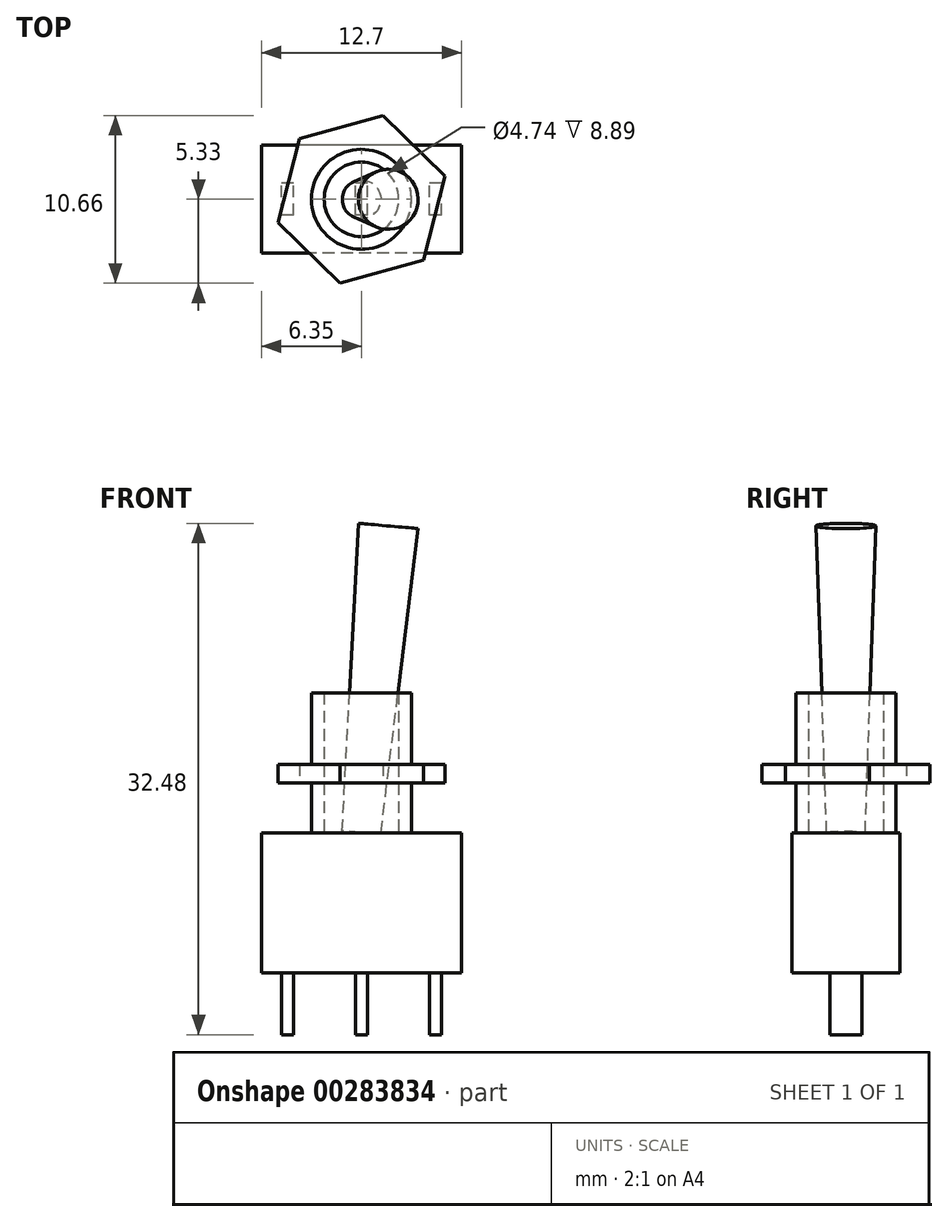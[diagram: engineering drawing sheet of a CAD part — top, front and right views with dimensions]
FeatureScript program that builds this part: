
annotation { "Feature Type Name" : "Feature", "Feature Type Description" : "" }
export const myFeature = defineFeature(function(context is Context, id is Id, definition is map)
    precondition{}
    {
        {
            var Q0;
            Q0=qCreatedBy(makeId("Top.planeOp"),FACE);
            var sketch = newSketch(context, id + "F0", { "sketchPlane" : qUnion([Q0])});
            skCircle(sketch, "E0", {"center": v(0, 0) * mm, "radius": 3.18 * mm});
            skCircle(sketch, "E1", {"center": v(0, 0) * mm, "radius": 2.37 * mm});
            skSolve(sketch);
        }
        {
            var Q0;
            Q0=makeQuery(id+"F0.imprint","IMPRINT",FACE,{"disambiguationData":[TD([[makeQuery(id+"F0.imprint","IMPRINT",EDGE,{"derivedFrom":sQuery(id+"F0.wireOp",EDGE,"E0")}),1.0]])]});
            extrude(context, id + "F1", {"entities" : qUnion([Q0]), "depth" : 8.9 * mm});
        }
        {
            var Q0;
            Q0=makeQuery(id+"F1.opExtrude","CAP_FACE",FACE,{"disambiguationData":[OSD([sQuery(id+"F0.wireOp",EDGE,"E0"),sQuery(id+"F0.wireOp",EDGE,"E1")])],"isStart":true});
            var sketch = newSketch(context, id + "F2", { "sketchPlane" : qUnion([Q0])});
            skLineSegment(sketch, "E2.bottom", {"start": v(6.35, -3.43) * mm, "end": v(-6.35, -3.43) * mm});
            skLineSegment(sketch, "E2.top", {"start": v(6.35, 3.43) * mm, "end": v(-6.35, 3.43) * mm});
            skLineSegment(sketch, "E2.left", {"start": v(6.35, -3.43) * mm, "end": v(6.35, 3.43) * mm});
            skLineSegment(sketch, "E2.right", {"start": v(-6.35, -3.43) * mm, "end": v(-6.35, 3.43) * mm});
            skPoint(sketch, "E2.middle", {"position": v(0, 0) * mm});
            skSolve(sketch);
        }
        {
            var Q0;
            Q0 = qSketchRegion(id + "F2", true);
            extrude(context, id + "F3", {"entities" : qUnion([Q0]), "operationType" : NewBodyOperationType.ADD, "depth" : 8.9 * mm});
        }
        {
            var Q0;
            Q0=makeQuery(id+"F3.opExtrude","CAP_FACE",FACE,{"disambiguationData":[OSD([sQuery(id+"F2.wireOp",EDGE,"E2.bottom"),sQuery(id+"F2.wireOp",EDGE,"E2.top"),sQuery(id+"F2.wireOp",EDGE,"E2.left"),sQuery(id+"F2.wireOp",EDGE,"E2.right")])],"isStart":false});
            var sketch = newSketch(context, id + "F4", { "sketchPlane" : qUnion([Q0])});
            skLineSegment(sketch, "E3.bottom", {"start": v(-4.32, 1.02) * mm, "end": v(-5.08, 1.02) * mm});
            skLineSegment(sketch, "E3.top", {"start": v(-4.32, -1.02) * mm, "end": v(-5.08, -1.02) * mm});
            skLineSegment(sketch, "E3.left", {"start": v(-4.32, 1.02) * mm, "end": v(-4.32, -1.02) * mm});
            skLineSegment(sketch, "E3.right", {"start": v(-5.08, 1.02) * mm, "end": v(-5.08, -1.02) * mm});
            skPoint(sketch, "E3.middle", {"position": v(0, 0) * mm});
            skPoint(sketch, "E3.middle.positionSnap0", {"position": v(-6.35, 0) * mm});
            skPoint(sketch, "E3.middle.positionSnap1", {"position": v(0, 3.43) * mm});
            skPoint(sketch, "E3.centerSnap0", {"position": v(-6.35, 0) * mm});
            skPoint(sketch, "E3.centerSnap1", {"position": v(0, 3.43) * mm});
            skLineSegment(sketch, "E4.1.0.0", {"start": v(-0.38, 1.02) * mm, "end": v(-0.38, -1.02) * mm});
            skLineSegment(sketch, "E4.1.0.1", {"start": v(0.38, 1.02) * mm, "end": v(0.38, -1.02) * mm});
            skLineSegment(sketch, "E4.1.0.2", {"start": v(0.38, -1.02) * mm, "end": v(-0.38, -1.02) * mm});
            skLineSegment(sketch, "E4.1.0.3", {"start": v(0.38, 1.02) * mm, "end": v(-0.38, 1.02) * mm});
            skPoint(sketch, "E4.1.0.4", {"position": v(4.7, 0) * mm});
            skLineSegment(sketch, "E4.2.0.0", {"start": v(4.32, 1.02) * mm, "end": v(4.32, -1.02) * mm});
            skLineSegment(sketch, "E4.2.0.1", {"start": v(5.08, 1.02) * mm, "end": v(5.08, -1.02) * mm});
            skLineSegment(sketch, "E4.2.0.2", {"start": v(5.08, -1.02) * mm, "end": v(4.32, -1.02) * mm});
            skLineSegment(sketch, "E4.2.0.3", {"start": v(5.08, 1.02) * mm, "end": v(4.32, 1.02) * mm});
            skPoint(sketch, "E4.2.0.4", {"position": v(9.4, 0) * mm});
            skLineSegment(sketch, "E4.direction1", {"start": v(-5.08, -1.02) * mm, "end": v(-0.38, -1.02) * mm, "construction": true});
            skLineSegment(sketch, "E5", {"start": v(0, 3.43) * mm, "end": v(0, 1.02) * mm, "construction": true});
            skLineSegment(sketch, "E6", {"start": v(0, -3.43) * mm, "end": v(0, -1.02) * mm, "construction": true});
            skSolve(sketch);
        }
        {
            var Q0;
            Q0 = qSketchRegion(id + "F4", true);
            extrude(context, id + "F5", {"entities" : qUnion([Q0]), "operationType" : NewBodyOperationType.ADD, "depth" : 3.94 * mm});
        }
        {
            var Q0;
            {var subQ0=sQuery(id+"F2.wireOp",EDGE,"E2.left");var subQ1=sQuery(id+"F2.wireOp",EDGE,"E2.top");var subQ2=sQuery(id+"F2.wireOp",EDGE,"E2.bottom");var subQ3=sQuery(id+"F2.wireOp",EDGE,"E2.right");Q0=makeQuery(id+"F3.boolean.opBoolean","SPLIT",FACE,{"disambiguationData":[TD([makeQuery(id+"F1.opExtrude","SWEPT_FACE",FACE,{"disambiguationData":[OSD([sQuery(id+"F0.wireOp",EDGE,"E0")])]})])],"derivedFrom":makeQuery(id+"F3.opExtrude","CAP_FACE",FACE,{"disambiguationData":[OSD([subQ2,subQ1,subQ0,subQ3])],"isStart":true})});}
            cPlane(context, id + "F6", {"entities" : qUnion([Q0]), "cplaneType" : CPlaneType.OFFSET, "offset" : 3.17 * mm, "width" : 152.4 * mm, "height" : 152.4 * mm});
        }
        {
            var Q0;
            Q0=qCreatedBy(id+"F6.planeOp",FACE);
            var sketch = newSketch(context, id + "F7", { "sketchPlane" : qUnion([Q0])});
            skCircle(sketch, "E7.cCircle", {"center": v(0, 0) * mm, "radius": 4.76 * mm, "construction": true});
            skLineSegment(sketch, "E7.0", {"start": v(-1.37, -5.33) * mm, "end": v(-5.3, -1.48) * mm});
            skLineSegment(sketch, "E7.1", {"start": v(-5.3, -1.48) * mm, "end": v(-3.93, 3.85) * mm});
            skLineSegment(sketch, "E7.2", {"start": v(-3.93, 3.85) * mm, "end": v(1.37, 5.33) * mm});
            skLineSegment(sketch, "E7.3", {"start": v(1.37, 5.33) * mm, "end": v(5.3, 1.48) * mm});
            skLineSegment(sketch, "E7.4", {"start": v(5.3, 1.48) * mm, "end": v(3.93, -3.85) * mm});
            skLineSegment(sketch, "E7.5", {"start": v(3.93, -3.85) * mm, "end": v(-1.37, -5.33) * mm});
            skPoint(sketch, "E7.0.midPoint", {"position": v(-3.33, -3.4) * mm});
            skCircle(sketch, "E8", {"center": v(0, 0) * mm, "radius": 3.18 * mm});
            skSolve(sketch);
        }
        {
            var Q0;
            Q0 = qSketchRegion(id + "F7", true);
            extrude(context, id + "F8", {"entities" : qUnion([Q0]), "operationType" : NewBodyOperationType.ADD, "depth" : 1.17 * mm});
        }
        {
            var Q0;
            {var subQ0=sQuery(id+"F2.wireOp",EDGE,"E2.left");var subQ1=sQuery(id+"F2.wireOp",EDGE,"E2.top");var subQ2=sQuery(id+"F2.wireOp",EDGE,"E2.bottom");var subQ3=sQuery(id+"F2.wireOp",EDGE,"E2.right");Q0=makeQuery(id+"F3.boolean.opBoolean","SPLIT",FACE,{"disambiguationData":[TD([makeQuery(id+"F1.opExtrude","SWEPT_FACE",FACE,{"disambiguationData":[OSD([sQuery(id+"F0.wireOp",EDGE,"E0")])]})])],"derivedFrom":makeQuery(id+"F3.opExtrude","CAP_FACE",FACE,{"disambiguationData":[OSD([subQ2,subQ1,subQ0,subQ3])],"isStart":true})});}
            var sketch = newSketch(context, id + "F9", { "sketchPlane" : qUnion([Q0])});
            skLineSegment(sketch, "E9", {"start": v(0, 3.43) * mm, "end": v(0, -3.43) * mm, "construction": true});
            skSolve(sketch);
        }
        {
            var Q0;
            Q0=sQuery(id+"F9.wireOp",EDGE,"E9");
            cPlane(context, id + "F10", {"entities" : qUnion([Q0]), "cplaneType" : CPlaneType.LINE_ANGLE, "offset" : 25.4 * mm, "angle" : 5 * degree, "oppositeDirection" : true, "width" : 152.4 * mm, "height" : 152.4 * mm});
        }
        {
            var Q0;
            Q0=qCreatedBy(id+"F10.planeOp",FACE);
            var sketch = newSketch(context, id + "F11", { "sketchPlane" : qUnion([Q0])});
            skCircle(sketch, "E10", {"center": v(0, 0) * mm, "radius": 1.22 * mm});
            skSolve(sketch);
        }
        {
            var Q0;
            Q0 = qSketchRegion(id + "F11", true);
            extrude(context, id + "F12", {"entities" : qUnion([Q0]), "operationType" : NewBodyOperationType.ADD, "oppositeDirection" : true, "depth" : 19.56 * mm, "hasDraft" : true, "draftAngle" : 2 * degree});
        }
    });
